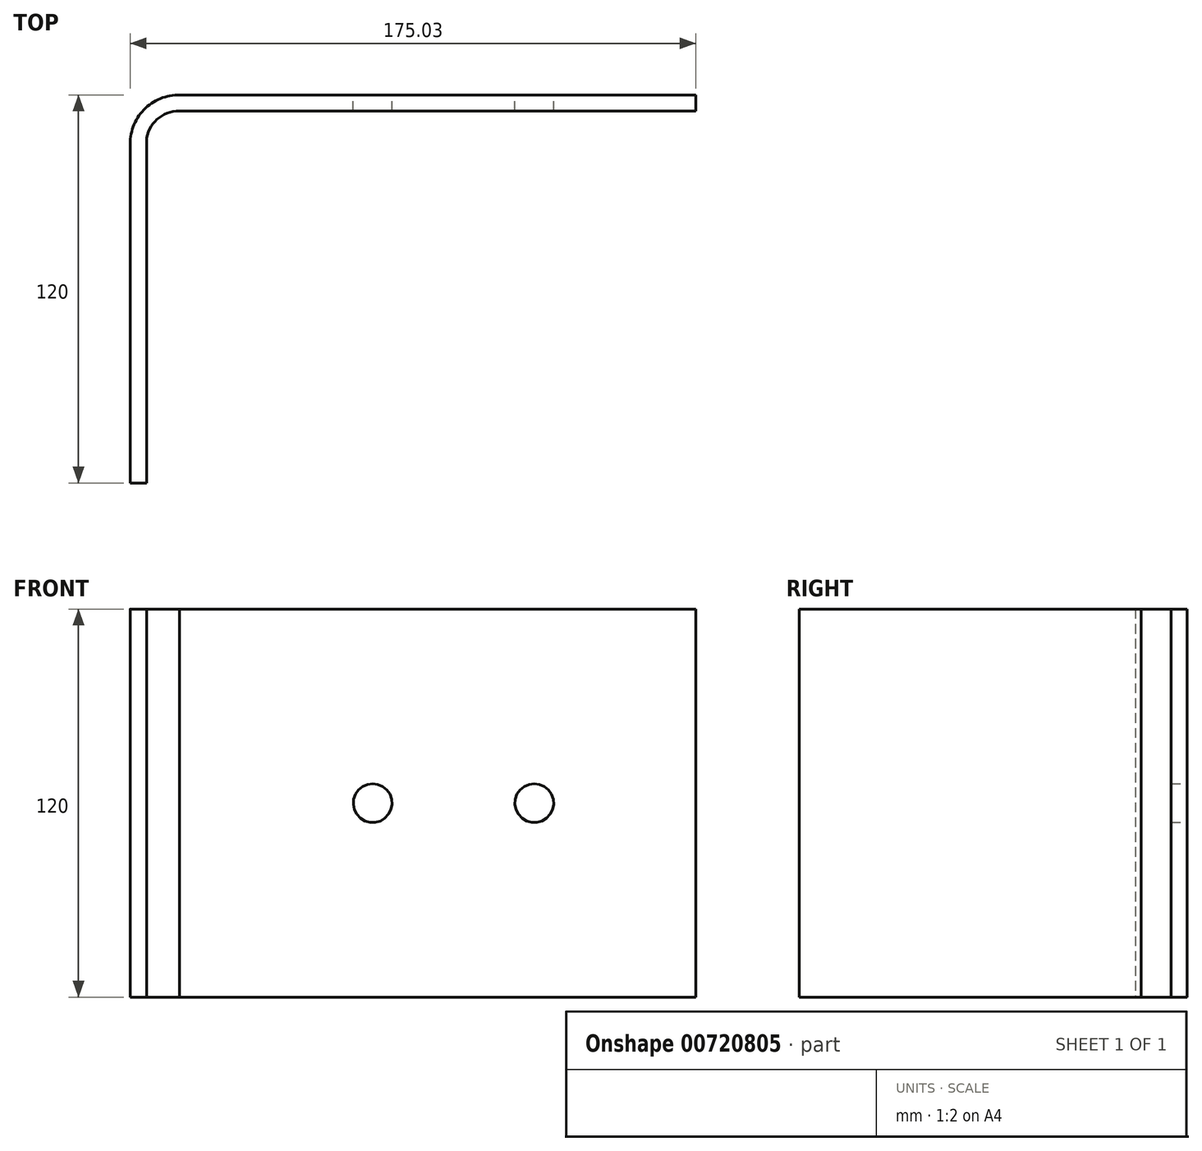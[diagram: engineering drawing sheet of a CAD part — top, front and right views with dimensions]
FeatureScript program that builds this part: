
annotation { "Feature Type Name" : "Feature", "Feature Type Description" : "" }
export const myFeature = defineFeature(function(context is Context, id is Id, definition is map)
    precondition{}
    {
        {
            var Q0;
            Q0=qCreatedBy(makeId("Top.planeOp"),FACE);
            var sketch = newSketch(context, id + "F0", { "sketchPlane" : qUnion([Q0])});
            skArc(sketch, "E0", {"start": v(-28.38, 31.77) * mm, "mid": v(-28.38, 31.77) * mm, "end": v(-28.38, 31.77) * mm});
            skLineSegment(sketch, "E1", {"start": v(-39.18, 36.77) * mm, "end": v(120.46, 36.77) * mm});
            skLineSegment(sketch, "E2", {"start": v(-54.54, 20.82) * mm, "end": v(-54.54, -83.23) * mm});
            skArc(sketch, "E3.0", {"start": v(-39.34, 31.77) * mm, "mid": v(-46.28, 29.18) * mm, "end": v(-49.54, 22.53) * mm});
            skLineSegment(sketch, "E4", {"start": v(-49.54, 22.53) * mm, "end": v(-49.54, -83.23) * mm});
            skLineSegment(sketch, "E5", {"start": v(-49.54, -83.23) * mm, "end": v(-54.54, -83.23) * mm});
            skLineSegment(sketch, "E6", {"start": v(-39.34, 31.77) * mm, "end": v(120.46, 31.77) * mm});
            skLineSegment(sketch, "E7", {"start": v(120.46, 31.77) * mm, "end": v(120.46, 36.77) * mm});
            skArc(sketch, "E8.trimOffspring", {"start": v(-49.54, 10.56) * mm, "mid": v(-49.54, 10.56) * mm, "end": v(-49.54, 10.56) * mm});
            skArc(sketch, "E9.trimOffspring", {"start": v(-39.18, 36.77) * mm, "mid": v(-50.37, 32.17) * mm, "end": v(-54.54, 20.82) * mm});
            skSolve(sketch);
        }
        {
            var Q0;
            Q0=qSketchRegion(id+"F0",true);
            extrude(context, id + "F1", {"entities" : qUnion([Q0]), "depth" : 120 * mm, "offsetDistance" : 25 * mm});
        }
        {
            var Q0;
            Q0=makeQuery(id+"F1.opExtrude","SWEPT_FACE",FACE,{"disambiguationData":[OSD([sQuery(id+"F0.wireOp",EDGE,"E1")])]});
            var sketch = newSketch(context, id + "F2", { "sketchPlane" : qUnion([Q0])});
            skCircle(sketch, "E10", {"center": v(-70.46, 60) * mm, "radius": 6 * mm});
            skCircle(sketch, "E11", {"center": v(-20.46, 60) * mm, "radius": 6 * mm});
            skSolve(sketch);
        }
        {
            var Q0;
            Q0=makeQuery(id+"F2.imprint","IMPRINT",FACE,{"disambiguationData":[TD([[makeQuery(id+"F2.imprint","IMPRINT",EDGE,{"derivedFrom":sQuery(id+"F2.wireOp",EDGE,"E10")}),1.0]])]});
            var Q1;
            Q1=makeQuery(id+"F2.imprint","IMPRINT",FACE,{"disambiguationData":[TD([[makeQuery(id+"F2.imprint","IMPRINT",EDGE,{"derivedFrom":sQuery(id+"F2.wireOp",EDGE,"E11")}),1.0]])]});
            var Q2;
            Q2=sQuery(id+"F2.wireOp",EDGE,"E11");
            var Q3;
            Q3=sQuery(id+"F2.wireOp",EDGE,"E10");
            extrude(context, id + "F3", {"entities" : qUnion([Q0, Q1]), "operationType" : NewBodyOperationType.REMOVE, "surfaceEntities" : qUnion([Q2, Q3]), "oppositeDirection" : true, "depth" : 5 * mm, "offsetDistance" : 25 * mm});
        }
        {
            var Q0;
            Q0=makeQuery(id+"F1.opExtrude","SWEPT_FACE",FACE,{"disambiguationData":[OSD([sQuery(id+"F0.wireOp",EDGE,"E4")])]});
            var sketch = newSketch(context, id + "F4", { "sketchPlane" : qUnion([Q0])});
            skLineSegment(sketch, "E12", {"start": v(-7.47, 160.68) * mm, "end": v(-347.47, 160.68) * mm});
            skLineSegment(sketch, "E13", {"start": v(-377.47, 190.68) * mm, "end": v(-377.47, 240.68) * mm});
            skLineSegment(sketch, "E14", {"start": v(-357.47, 260.68) * mm, "end": v(-147.47, 260.68) * mm});
            skLineSegment(sketch, "E15", {"start": v(-127.47, 280.68) * mm, "end": v(-127.47, 380.68) * mm});
            skLineSegment(sketch, "E16", {"start": v(-97.47, 410.68) * mm, "end": v(-7.47, 410.68) * mm});
            skLineSegment(sketch, "E17", {"start": v(22.53, 380.68) * mm, "end": v(22.53, 190.68) * mm});
            skPoint(sketch, "E18.visualSharp", {"position": v(-127.47, 410.68) * mm});
            skArc(sketch, "E18.filletArc", {"start": v(-97.47, 410.68) * mm, "mid": v(-118.68, 401.9) * mm, "end": v(-127.47, 380.68) * mm});
            skPoint(sketch, "E19.visualSharp", {"position": v(22.53, 410.68) * mm});
            skArc(sketch, "E19.filletArc", {"start": v(22.53, 380.68) * mm, "mid": v(13.74, 401.9) * mm, "end": v(-7.47, 410.68) * mm});
            skPoint(sketch, "E20.visualSharp", {"position": v(22.53, 160.68) * mm});
            skArc(sketch, "E20.filletArc", {"start": v(-7.47, 160.68) * mm, "mid": v(13.74, 169.47) * mm, "end": v(22.53, 190.68) * mm});
            skPoint(sketch, "E21.visualSharp", {"position": v(-377.47, 160.68) * mm});
            skArc(sketch, "E21.filletArc", {"start": v(-377.47, 190.68) * mm, "mid": v(-368.68, 169.47) * mm, "end": v(-347.47, 160.68) * mm});
            skPoint(sketch, "E22.visualSharp", {"position": v(-377.47, 260.68) * mm});
            skArc(sketch, "E22.filletArc", {"start": v(-357.47, 260.68) * mm, "mid": v(-371.61, 254.82) * mm, "end": v(-377.47, 240.68) * mm});
            skPoint(sketch, "E23.visualSharp", {"position": v(-127.47, 260.68) * mm});
            skArc(sketch, "E23.filletArc", {"start": v(-147.47, 260.68) * mm, "mid": v(-133.33, 266.54) * mm, "end": v(-127.47, 280.68) * mm});
            skCircle(sketch, "E24", {"center": v(-87.47, 360.68) * mm, "radius": 6 * mm});
            skCircle(sketch, "E25", {"center": v(-7.47, 360.68) * mm, "radius": 6 * mm});
            skSolve(sketch);
        }
        {
            var Q0;
            Q0=qSketchRegion(id+"F4",true);
            extrude(context, id + "F5", {"entities" : qUnion([Q0]), "depth" : 5 * mm, "offsetDistance" : 25 * mm});
        }
        {
            var Q0;
            Q0=makeQuery(id+"F5.opExtrude","SWEPT_BODY",BODY,{"disambiguationData":[OSD([sQuery(id+"F4.wireOp",EDGE,"E12"),sQuery(id+"F4.wireOp",EDGE,"E13"),sQuery(id+"F4.wireOp",EDGE,"E14"),sQuery(id+"F4.wireOp",EDGE,"E15"),sQuery(id+"F4.wireOp",EDGE,"E16"),sQuery(id+"F4.wireOp",EDGE,"E17"),sQuery(id+"F4.wireOp",EDGE,"E18.filletArc"),sQuery(id+"F4.wireOp",EDGE,"E19.filletArc"),sQuery(id+"F4.wireOp",EDGE,"E20.filletArc"),sQuery(id+"F4.wireOp",EDGE,"E21.filletArc"),sQuery(id+"F4.wireOp",EDGE,"E22.filletArc"),sQuery(id+"F4.wireOp",EDGE,"E23.filletArc"),sQuery(id+"F4.wireOp",EDGE,"E24"),sQuery(id+"F4.wireOp",EDGE,"E25")])]});
            deleteBodies(context, id + "F6", {"entities" : qUnion([Q0])});
        }
    });
